annotation { "Feature Type Name" : "Feature", "Feature Type Description" : "" }
export const myFeature = defineFeature(function(context is Context, id is Id, definition is map)
    precondition{}
    {
        {
            var Q0;
            Q0=qCreatedBy(makeId("Top.planeOp"),FACE);
            var sketch = newSketch(context, id + "F0", { "sketchPlane" : qUnion([Q0])});
            skLineSegment(sketch, "E0.bottom", {"start": v(0, 0) * mm, "end": v(63.5, 0) * mm});
            skLineSegment(sketch, "E0.top", {"start": v(0, 19.05) * mm, "end": v(63.5, 19.05) * mm});
            skLineSegment(sketch, "E0.left", {"start": v(0, 0) * mm, "end": v(0, 19.05) * mm});
            skLineSegment(sketch, "E0.right", {"start": v(63.5, 0) * mm, "end": v(63.5, 19.05) * mm});
            skSolve(sketch);
        }
        {
            var Q0;
            Q0 = qSketchRegion(id + "F0", true);
            extrude(context, id + "F1", {"entities" : qUnion([Q0]), "depth" : 3.8 * mm, "offsetDistance" : 25.4 * mm});
        }
        {
            var Q0;
            Q0=makeQuery(id+"F1.opExtrude","CAP_FACE",FACE,{"disambiguationData":[OSD([sQuery(id+"F0.wireOp",EDGE,"E0.bottom"),sQuery(id+"F0.wireOp",EDGE,"E0.top"),sQuery(id+"F0.wireOp",EDGE,"E0.left"),sQuery(id+"F0.wireOp",EDGE,"E0.right")])],"isStart":false});
            var sketch = newSketch(context, id + "F2", { "sketchPlane" : qUnion([Q0])});
            skLineSegment(sketch, "E1", {"start": v(13.76, 12.35) * mm, "end": v(15.92, 12.35) * mm});
            skLineSegment(sketch, "E2", {"start": v(15.92, 12.35) * mm, "end": v(15.92, 16.23) * mm});
            skLineSegment(sketch, "E3", {"start": v(15.92, 16.23) * mm, "end": v(13.67, 16.23) * mm});
            skLineSegment(sketch, "E4", {"start": v(13.67, 16.23) * mm, "end": v(13.67, 15.15) * mm});
            skArc(sketch, "E5", {"start": v(13.67, 15.15) * mm, "mid": v(12.75, 15.6) * mm, "end": v(11.77, 15.9) * mm});
            skArc(sketch, "E6", {"start": v(11.77, 15.9) * mm, "mid": v(11, 16.12) * mm, "end": v(10.18, 16.16) * mm});
            skArc(sketch, "E7", {"start": v(10.18, 16.16) * mm, "mid": v(10.04, 16.2) * mm, "end": v(9.9, 16.16) * mm});
            skArc(sketch, "E8", {"start": v(9.9, 16.16) * mm, "mid": v(8.81, 16.18) * mm, "end": v(7.74, 15.96) * mm});
            skArc(sketch, "E9", {"start": v(7.74, 15.96) * mm, "mid": v(7.3, 15.87) * mm, "end": v(6.88, 15.7) * mm});
            skArc(sketch, "E10", {"start": v(6.88, 15.7) * mm, "mid": v(6.53, 15.55) * mm, "end": v(6.19, 15.37) * mm});
            skArc(sketch, "E11", {"start": v(6.19, 15.37) * mm, "mid": v(5.86, 15.2) * mm, "end": v(5.57, 14.97) * mm});
            skArc(sketch, "E12", {"start": v(5.57, 14.97) * mm, "mid": v(5.15, 14.7) * mm, "end": v(4.74, 14.4) * mm});
            skArc(sketch, "E13", {"start": v(4.74, 14.4) * mm, "mid": v(4.25, 13.92) * mm, "end": v(3.82, 13.4) * mm});
            skArc(sketch, "E14", {"start": v(3.82, 13.4) * mm, "mid": v(3.51, 12.98) * mm, "end": v(3.24, 12.54) * mm});
            skArc(sketch, "E15", {"start": v(3.24, 12.54) * mm, "mid": v(3.02, 12.05) * mm, "end": v(2.85, 11.54) * mm});
            skArc(sketch, "E16", {"start": v(2.85, 11.54) * mm, "mid": v(2.76, 11.14) * mm, "end": v(2.69, 10.73) * mm});
            skArc(sketch, "E17", {"start": v(2.69, 9.66) * mm, "mid": v(2.83, 9.13) * mm, "end": v(3.05, 8.62) * mm});
            skArc(sketch, "E18", {"start": v(3.05, 8.62) * mm, "mid": v(3.32, 8.04) * mm, "end": v(3.63, 7.48) * mm});
            skArc(sketch, "E19", {"start": v(3.63, 7.48) * mm, "mid": v(4.12, 6.87) * mm, "end": v(4.74, 6.39) * mm});
            skArc(sketch, "E20", {"start": v(4.74, 6.39) * mm, "mid": v(5.22, 5.96) * mm, "end": v(5.78, 5.64) * mm});
            skArc(sketch, "E21", {"start": v(5.78, 5.64) * mm, "mid": v(6.47, 5.32) * mm, "end": v(7.18, 5.09) * mm});
            skArc(sketch, "E22", {"start": v(7.18, 5.09) * mm, "mid": v(7.93, 4.92) * mm, "end": v(8.68, 4.8) * mm});
            skArc(sketch, "E23", {"start": v(8.68, 4.8) * mm, "mid": v(9.14, 4.77) * mm, "end": v(9.6, 4.8) * mm});
            skArc(sketch, "E24", {"start": v(9.6, 4.8) * mm, "mid": v(10.2, 4.84) * mm, "end": v(10.8, 4.93) * mm});
            skArc(sketch, "E25", {"start": v(10.8, 4.93) * mm, "mid": v(11.66, 5.1) * mm, "end": v(12.52, 5.3) * mm});
            skArc(sketch, "E26", {"start": v(12.52, 5.3) * mm, "mid": v(13.11, 5.55) * mm, "end": v(13.7, 5.8) * mm});
            skLineSegment(sketch, "E27", {"start": v(13.7, 5.8) * mm, "end": v(13.7, 5.47) * mm});
            skLineSegment(sketch, "E28", {"start": v(16.15, 5.47) * mm, "end": v(16.15, 9.42) * mm});
            skLineSegment(sketch, "E29", {"start": v(16.15, 9.42) * mm, "end": v(16.78, 9.42) * mm});
            skLineSegment(sketch, "E30", {"start": v(16.78, 9.42) * mm, "end": v(16.78, 5) * mm});
            skLineSegment(sketch, "E31", {"start": v(16.78, 5) * mm, "end": v(15.5, 5) * mm});
            skLineSegment(sketch, "E32", {"start": v(15.5, 5) * mm, "end": v(15.5, 2.72) * mm});
            skLineSegment(sketch, "E33", {"start": v(15.5, 2.72) * mm, "end": v(20.93, 2.72) * mm});
            skLineSegment(sketch, "E34", {"start": v(20.93, 2.72) * mm, "end": v(20.93, 5.05) * mm});
            skLineSegment(sketch, "E35", {"start": v(20.93, 5.05) * mm, "end": v(19.73, 5.05) * mm});
            skLineSegment(sketch, "E36", {"start": v(19.73, 5.05) * mm, "end": v(19.73, 9.42) * mm});
            skLineSegment(sketch, "E37", {"start": v(19.73, 9.42) * mm, "end": v(22.22, 9.42) * mm});
            skLineSegment(sketch, "E38", {"start": v(22.22, 9.42) * mm, "end": v(22.42, 8.39) * mm});
            skLineSegment(sketch, "E39", {"start": v(22.42, 8.39) * mm, "end": v(24.5, 8.39) * mm});
            skLineSegment(sketch, "E40", {"start": v(24.5, 8.39) * mm, "end": v(24.5, 11.94) * mm});
            skLineSegment(sketch, "E41", {"start": v(24.5, 11.94) * mm, "end": v(15.7, 11.94) * mm});
            skLineSegment(sketch, "E42", {"start": v(15.7, 11.94) * mm, "end": v(11.25, 11.94) * mm});
            skLineSegment(sketch, "E43", {"start": v(11.25, 11.94) * mm, "end": v(11.25, 8.39) * mm});
            skLineSegment(sketch, "E44", {"start": v(11.25, 8.39) * mm, "end": v(13.27, 8.39) * mm});
            skLineSegment(sketch, "E45", {"start": v(13.27, 8.39) * mm, "end": v(13.48, 9.42) * mm});
            skLineSegment(sketch, "E46", {"start": v(13.48, 9.42) * mm, "end": v(14.04, 9.42) * mm});
            skArc(sketch, "E47", {"start": v(12.96, 7.8) * mm, "mid": v(13.6, 8.54) * mm, "end": v(14.04, 9.42) * mm});
            skArc(sketch, "E48", {"start": v(10.9, 7.05) * mm, "mid": v(11.99, 7.28) * mm, "end": v(12.96, 7.8) * mm});
            skArc(sketch, "E49", {"start": v(8.64, 7.33) * mm, "mid": v(9.76, 7.07) * mm, "end": v(10.9, 7.05) * mm});
            skArc(sketch, "E50", {"start": v(6.78, 8.6) * mm, "mid": v(7.61, 7.82) * mm, "end": v(8.64, 7.33) * mm});
            skArc(sketch, "E51", {"start": v(6.22, 10.12) * mm, "mid": v(6.37, 9.3) * mm, "end": v(6.78, 8.6) * mm});
            skArc(sketch, "E52", {"start": v(6.93, 12.27) * mm, "mid": v(6.36, 11.26) * mm, "end": v(6.22, 10.12) * mm});
            skArc(sketch, "E53", {"start": v(10.06, 13.73) * mm, "mid": v(8.34, 13.32) * mm, "end": v(6.93, 12.27) * mm});
            skArc(sketch, "E54", {"start": v(13.76, 12.35) * mm, "mid": v(12.03, 13.36) * mm, "end": v(10.06, 13.73) * mm});
            skLineSegment(sketch, "E55", {"start": v(13.7, 5.47) * mm, "end": v(16.15, 5.47) * mm});
            skArc(sketch, "E56", {"start": v(2.69, 10.73) * mm, "mid": v(2.64, 10.2) * mm, "end": v(2.69, 9.66) * mm});
            skSolve(sketch);
        }
        {
            var Q0;
            Q0 = qSketchRegion(id + "F2", true);
            extrude(context, id + "F3", {"entities" : qUnion([Q0]), "operationType" : NewBodyOperationType.REMOVE, "oppositeDirection" : true, "depth" : 3.8 * mm, "offsetDistance" : 25.4 * mm});
        }
        {
            var Q0;
            Q0=makeQuery(id+"F1.opExtrude","SWEPT_EDGE",EDGE,{"disambiguationData":[OSD([sQuery(id+"F0.wireOp",EDGE,"E0.bottom"),sQuery(id+"F0.wireOp",EDGE,"E0.right")])]});
            var Q1;
            Q1=makeQuery(id+"F1.opExtrude","SWEPT_EDGE",EDGE,{"disambiguationData":[OSD([sQuery(id+"F0.wireOp",EDGE,"E0.top"),sQuery(id+"F0.wireOp",EDGE,"E0.right")])]});
            chamfer(context, id + "F4", {"entities" : qUnion([Q0, Q1]), "width" : 5.08 * mm, "tangentPropagation" : true});
        }
        {
            var Q0;
            Q0=makeQuery(id+"F1.opExtrude","SWEPT_EDGE",EDGE,{"disambiguationData":[OSD([sQuery(id+"F0.wireOp",EDGE,"E0.bottom"),sQuery(id+"F0.wireOp",EDGE,"E0.left")])]});
            var Q1;
            Q1=makeQuery(id+"F1.opExtrude","SWEPT_EDGE",EDGE,{"disambiguationData":[OSD([sQuery(id+"F0.wireOp",EDGE,"E0.top"),sQuery(id+"F0.wireOp",EDGE,"E0.left")])]});
            fillet(context, id + "F5", {"entities" : qUnion([Q0, Q1]), "radius" : 7.62 * mm, "tangentPropagation" : true, "allowEdgeOverflow" : false});
        }
        {
            var Q0;
            Q0=makeQuery(id+"F1.opExtrude","CAP_FACE",FACE,{"disambiguationData":[OSD([sQuery(id+"F0.wireOp",EDGE,"E0.bottom"),sQuery(id+"F0.wireOp",EDGE,"E0.top"),sQuery(id+"F0.wireOp",EDGE,"E0.left"),sQuery(id+"F0.wireOp",EDGE,"E0.right")])],"isStart":false});
            var sketch = newSketch(context, id + "F6", { "sketchPlane" : qUnion([Q0])});
            skText(sketch, "E57", { "text": "Madison Walker\nGTRI-ATAS", "fontName": "OpenSans-Regular.ttf"});
            const initialGuessF6  = {"E57": [0.02856, 0.01092, 1, 0, 0.00284]};
            skSetInitialGuess(sketch, initialGuessF6);
            skSolve(sketch);
        }
        {
            var Q0;
            Q0 = qSketchRegion(id + "F6", true);
            extrude(context, id + "F7", {"entities" : qUnion([Q0]), "operationType" : NewBodyOperationType.REMOVE, "oppositeDirection" : true, "depth" : 2.54 * mm, "offsetDistance" : 25.4 * mm});
        }
        {
            var Q0;
            Q0=qCreatedBy(makeId("Right.planeOp"),FACE);
            var sketch = newSketch(context, id + "F8", { "sketchPlane" : qUnion([Q0])});
            skLineSegment(sketch, "E58.bottom", {"start": v(11.4, 3.84) * mm, "end": v(7.65, 3.84) * mm});
            skLineSegment(sketch, "E58.top", {"start": v(11.4, 0) * mm, "end": v(7.65, 0) * mm});
            skLineSegment(sketch, "E58.left", {"start": v(11.4, 3.84) * mm, "end": v(11.4, 0) * mm});
            skLineSegment(sketch, "E58.right", {"start": v(7.65, 3.84) * mm, "end": v(7.65, 0) * mm});
            skSolve(sketch);
        }
        {
            var Q0;
            Q0 = qSketchRegion(id + "F8", true);
            extrude(context, id + "F9", {"entities" : qUnion([Q0]), "operationType" : NewBodyOperationType.ADD, "depth" : -3.8 * mm, "offsetDistance" : 25.4 * mm});
        }
        {
            var Q0;
            Q0=makeQuery(id+"F9.opExtrude","SWEPT_FACE",FACE,{"disambiguationData":[OSD([sQuery(id+"F8.wireOp",EDGE,"E58.bottom")])]});
            var sketch = newSketch(context, id + "F10", { "sketchPlane" : qUnion([Q0])});
            skPoint(sketch, "E59", {"position": v(-1.9, 9.5) * mm});
            skCircle(sketch, "E60", {"center": v(-1.9, 9.5) * mm, "radius": 1.27 * mm});
            skSolve(sketch);
        }
        {
            var Q0;
            Q0=makeQuery(id+"F10.imprint","IMPRINT",FACE,{"disambiguationData":[TD([[makeQuery(id+"F10.imprint","IMPRINT",EDGE,{"derivedFrom":sQuery(id+"F10.wireOp",EDGE,"E60")}),1.0]])]});
            extrude(context, id + "F11", {"entities" : qUnion([Q0]), "operationType" : NewBodyOperationType.REMOVE, "oppositeDirection" : true, "depth" : 5080 * mm, "offsetDistance" : 25.4 * mm});
        }
    });